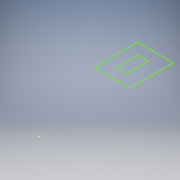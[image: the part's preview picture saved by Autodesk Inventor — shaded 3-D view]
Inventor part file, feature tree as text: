
AUTODESK INVENTOR PART (.ipt)
format: ipt  version: 2017 (Build 210142000, 142)  size: 84,992 bytes
history: native  units: mm
features: sketch x1
ambient origin geometry x8: Origin, YZ Plane, XZ Plane, XY Plane, X Axis, Y Axis, Z Axis, Center Point
feature tree (1):
  sketch  "Sketch1"
